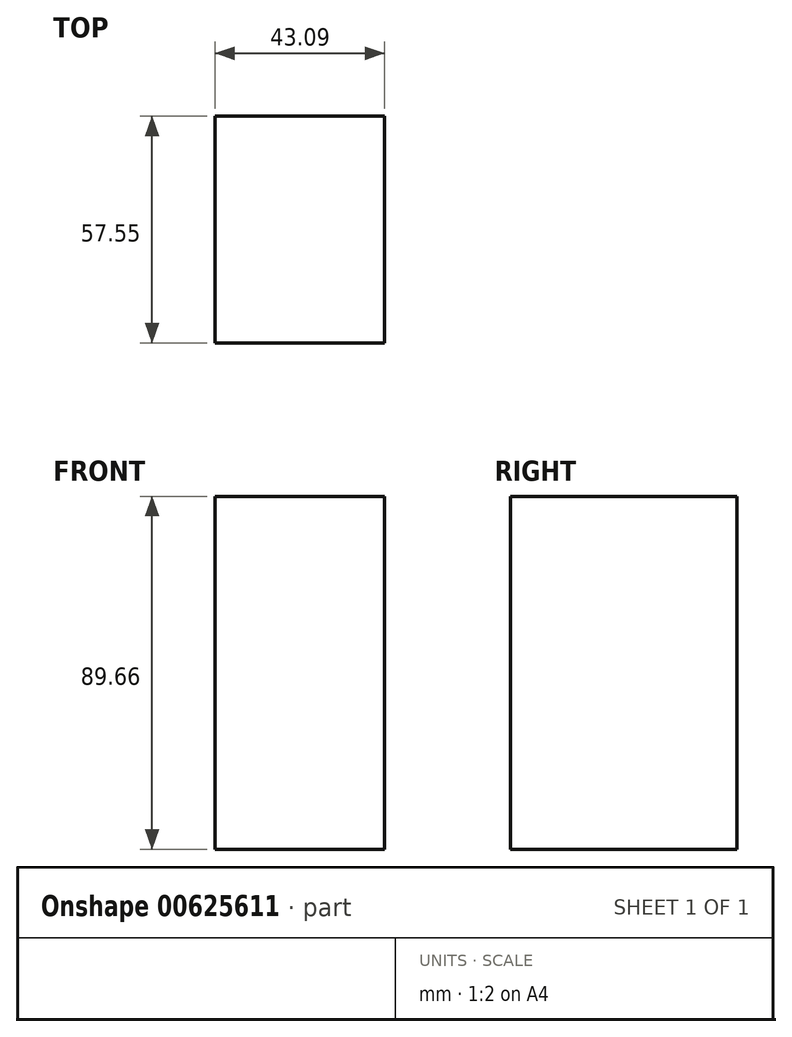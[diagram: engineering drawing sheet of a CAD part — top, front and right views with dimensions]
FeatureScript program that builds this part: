
annotation { "Feature Type Name" : "Feature", "Feature Type Description" : "" }
export const myFeature = defineFeature(function(context is Context, id is Id, definition is map)
    precondition{}
    {
        {
            var Q0;
            Q0=qCreatedBy(makeId("Top.planeOp"),FACE);
            var sketch = newSketch(context, id + "F0", { "sketchPlane" : qUnion([Q0])});
            skLineSegment(sketch, "E0.bottom", {"start": v(0, 0) * mm, "end": v(-43.09, 0) * mm});
            skLineSegment(sketch, "E0.top", {"start": v(0, 57.55) * mm, "end": v(-43.09, 57.55) * mm});
            skLineSegment(sketch, "E0.left", {"start": v(0, 0) * mm, "end": v(0, 57.55) * mm});
            skLineSegment(sketch, "E0.right", {"start": v(-43.09, 0) * mm, "end": v(-43.09, 57.55) * mm});
            skSolve(sketch);
        }
        {
            var Q0;
            Q0=makeQuery(id+"F0.imprint","IMPRINT",FACE,{"disambiguationData":[TD([[makeQuery(id+"F0.imprint","IMPRINT",EDGE,{"derivedFrom":sQuery(id+"F0.wireOp",EDGE,"E0.bottom")}),-1.0]])]});
            extrude(context, id + "F1", {"entities" : qUnion([Q0]), "depth" : 89.66 * mm, "offsetDistance" : 25.4 * mm});
        }
    });
